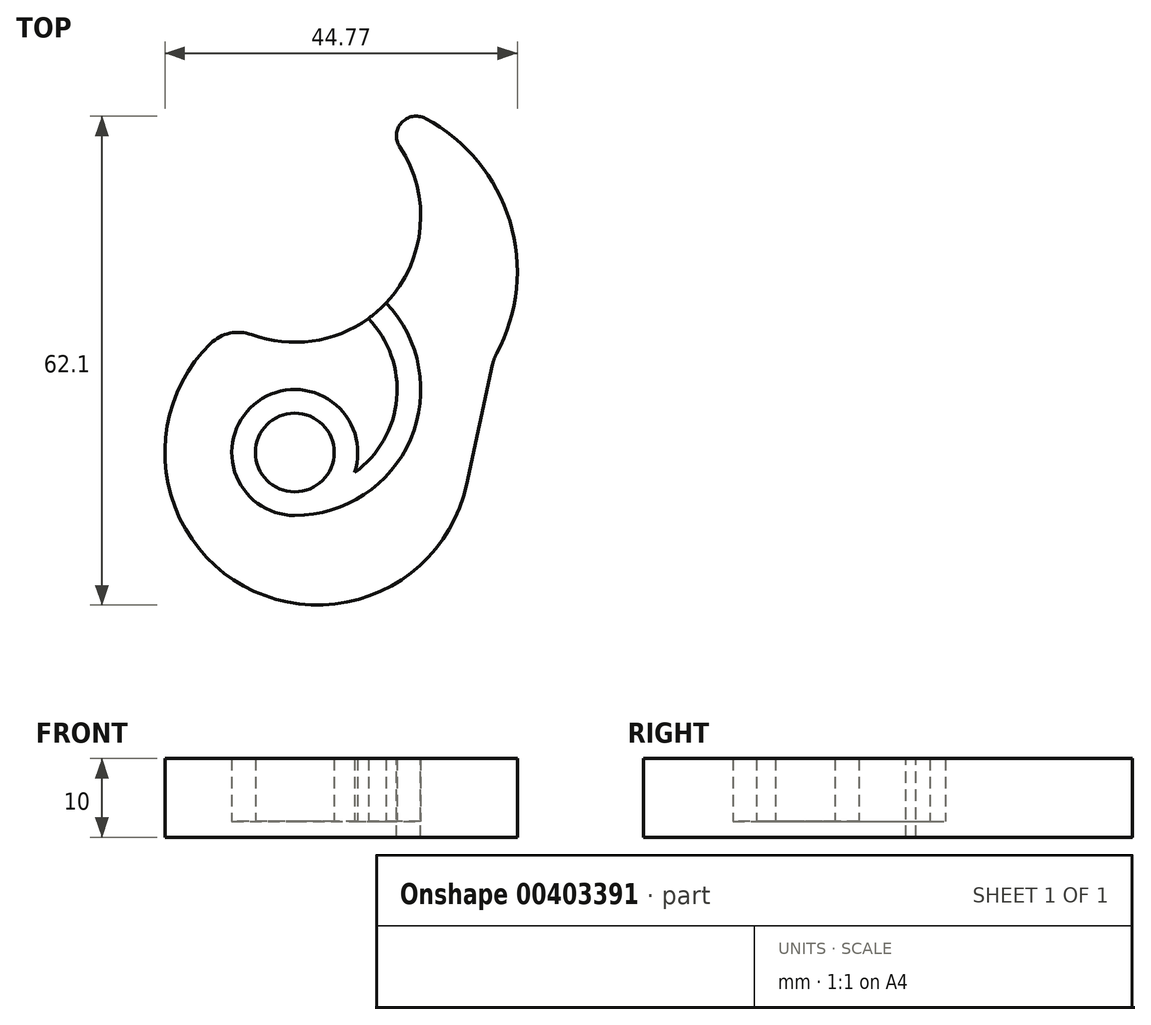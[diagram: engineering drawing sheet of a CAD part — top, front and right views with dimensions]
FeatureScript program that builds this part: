
annotation { "Feature Type Name" : "Feature", "Feature Type Description" : "" }
export const myFeature = defineFeature(function(context is Context, id is Id, definition is map)
    precondition{}
    {
        {
            var Q0;
            Q0=qCreatedBy(makeId("Top.planeOp"),FACE);
            var sketch = newSketch(context, id + "F0", { "sketchPlane" : qUnion([Q0])});
            skArc(sketch, "E0", {"start": v(-5.47, -15.03) * mm, "mid": v(2.2, -15.85) * mm, "end": v(9.36, -12.98) * mm});
            skArc(sketch, "E1", {"start": v(25.63, -17.44) * mm, "mid": v(27.33, -0.62) * mm, "end": v(16.6, 12.43) * mm});
            skArc(sketch, "E2", {"start": v(16.6, 12.43) * mm, "mid": v(13.57, 11.9) * mm, "end": v(13.34, 8.84) * mm});
            skCircle(sketch, "E3", {"center": v(0, -30) * mm, "radius": 5 * mm});
            skArc(sketch, "E4", {"start": v(7.58, -32.56) * mm, "mid": v(-4.66, -23.5) * mm, "end": v(0, -38) * mm});
            skArc(sketch, "E5", {"start": v(0, -38) * mm, "mid": v(14.7, -28.32) * mm, "end": v(11.62, -11) * mm});
            skArc(sketch, "E6.trimOffspring", {"start": v(7.58, -32.56) * mm, "mid": v(12.95, -23.18) * mm, "end": v(9.36, -12.98) * mm});
            skArc(sketch, "E7.trimOffspring", {"start": v(11.62, -11) * mm, "mid": v(15.94, -1.38) * mm, "end": v(13.34, 8.84) * mm});
            skPoint(sketch, "E8.visualSharp", {"position": v(11.62, -11) * mm});
            skPoint(sketch, "E9.visualSharp", {"position": v(9.36, -12.98) * mm});
            skArc(sketch, "E10", {"start": v(-10.68, -16.16) * mm, "mid": v(-6.5, -46.96) * mm, "end": v(21.81, -34.11) * mm});
            skLineSegment(sketch, "E11", {"start": v(25.15, -18.75) * mm, "end": v(21.81, -34.11) * mm});
            skPoint(sketch, "E12.visualSharp", {"position": v(-7.91, -13.9) * mm});
            skArc(sketch, "E12.filletArc", {"start": v(-5.47, -15.03) * mm, "mid": v(-8.24, -14.85) * mm, "end": v(-10.68, -16.16) * mm});
            skPoint(sketch, "E13.visualSharp", {"position": v(25.3, -18.03) * mm});
            skArc(sketch, "E13.filletArc", {"start": v(25.63, -17.44) * mm, "mid": v(25.34, -18.08) * mm, "end": v(25.15, -18.75) * mm});
            skSolve(sketch);
        }
        {
            var Q0;
            Q0=qCreatedBy(makeId("Top.planeOp"),FACE);
            var sketch = newSketch(context, id + "F1", { "sketchPlane" : qUnion([Q0])});
            skArc(sketch, "E14", {"start": v(-5.47, -15.03) * mm, "mid": v(12.57, -9.9) * mm, "end": v(13.34, 8.84) * mm});
            skArc(sketch, "E15", {"start": v(16.6, 12.43) * mm, "mid": v(13.57, 11.9) * mm, "end": v(13.34, 8.84) * mm});
            skArc(sketch, "E16", {"start": v(-10.68, -16.16) * mm, "mid": v(-6.5, -46.96) * mm, "end": v(21.81, -34.11) * mm});
            skLineSegment(sketch, "E17", {"start": v(21.81, -34.11) * mm, "end": v(25.15, -18.75) * mm});
            skArc(sketch, "E18", {"start": v(25.63, -17.44) * mm, "mid": v(27.33, -0.62) * mm, "end": v(16.6, 12.43) * mm});
            skPoint(sketch, "E19.visualSharp", {"position": v(25.3, -18.03) * mm});
            skArc(sketch, "E19.filletArc", {"start": v(25.63, -17.44) * mm, "mid": v(25.34, -18.08) * mm, "end": v(25.15, -18.75) * mm});
            skPoint(sketch, "E20.visualSharp", {"position": v(-7.91, -13.9) * mm});
            skArc(sketch, "E20.filletArc", {"start": v(-5.47, -15.03) * mm, "mid": v(-8.24, -14.85) * mm, "end": v(-10.68, -16.16) * mm});
            skSolve(sketch);
        }
        {
            var Q0;
            Q0 = qSketchRegion(id + "F1", true);
            extrude(context, id + "F2", {"entities" : qUnion([Q0]), "oppositeDirection" : true, "depth" : 2 * mm});
        }
        {
            var Q0;
            Q0 = qSketchRegion(id + "F0", true);
            extrude(context, id + "F3", {"entities" : qUnion([Q0]), "operationType" : NewBodyOperationType.ADD, "depth" : 8 * mm});
        }
    });
